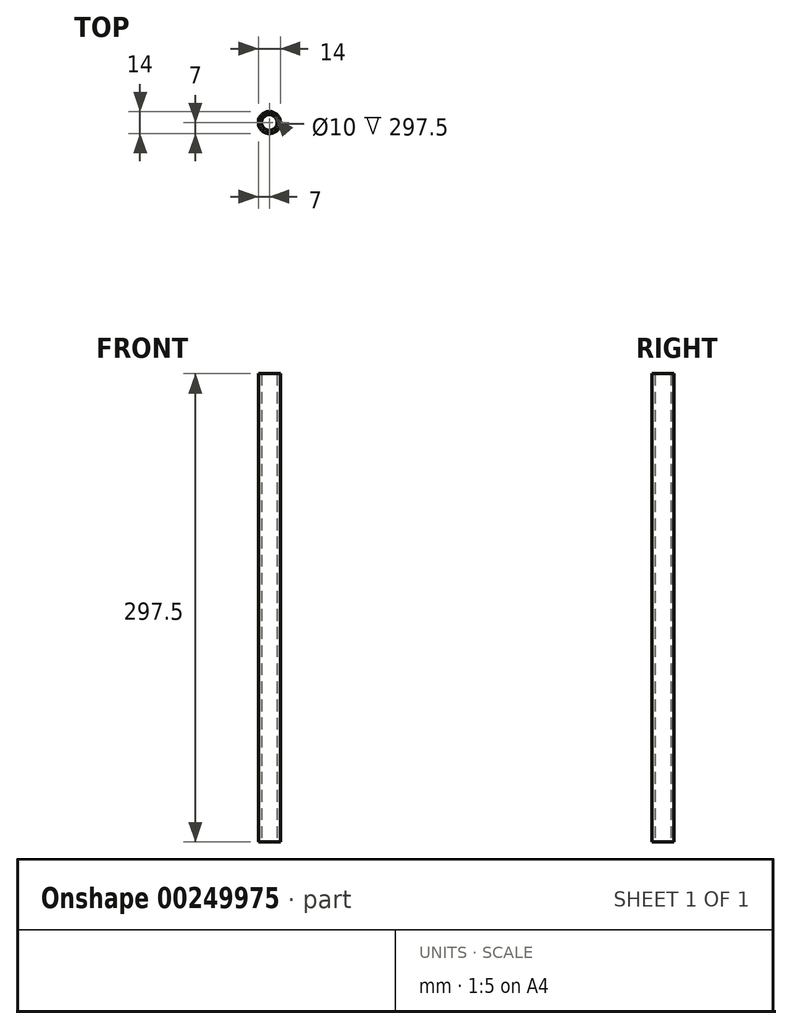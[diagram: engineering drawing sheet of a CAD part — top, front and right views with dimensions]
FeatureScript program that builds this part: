
annotation { "Feature Type Name" : "Feature", "Feature Type Description" : "" }
export const myFeature = defineFeature(function(context is Context, id is Id, definition is map)
    precondition{}
    {
        {
            var Q0;
            Q0=qCreatedBy(makeId("Top.planeOp"),FACE);
            var sketch = newSketch(context, id + "F0", { "sketchPlane" : qUnion([Q0])});
            skCircle(sketch, "E0", {"center": v(0, 0) * mm, "radius": 5 * mm});
            skCircle(sketch, "E1", {"center": v(0, 0) * mm, "radius": 7 * mm});
            skSolve(sketch);
        }
        {
            var Q0;
            Q0 = qSketchRegion(id + "F0", true);
            extrude(context, id + "F1", {"entities" : qUnion([Q0]), "depth" : 297.5 * mm});
        }
    });
